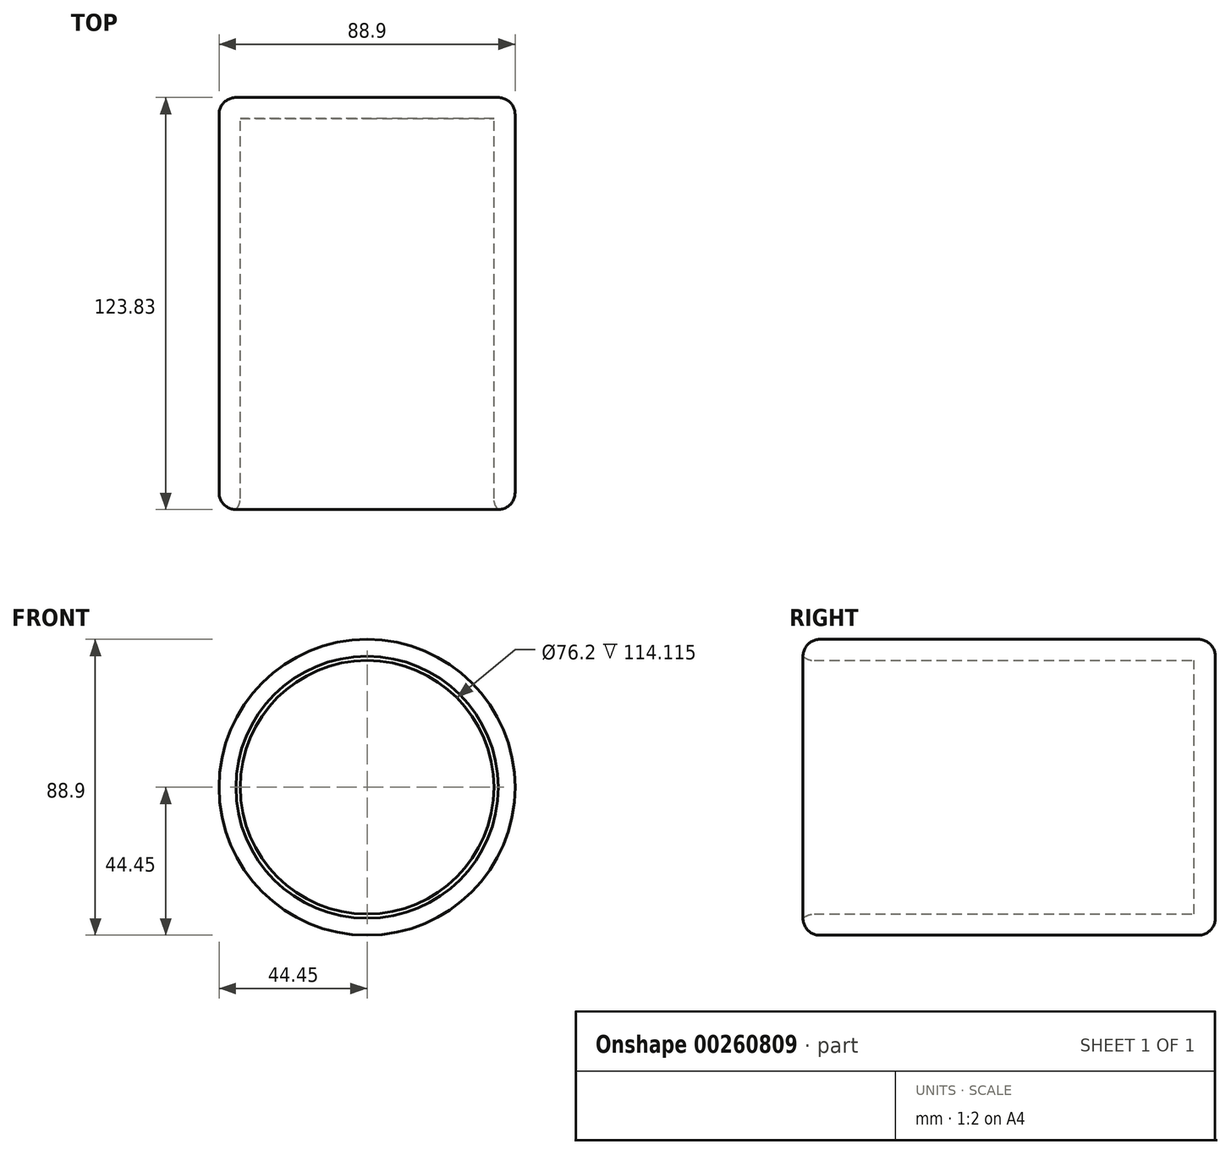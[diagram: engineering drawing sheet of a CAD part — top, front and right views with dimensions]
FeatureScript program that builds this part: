
annotation { "Feature Type Name" : "Feature", "Feature Type Description" : "" }
export const myFeature = defineFeature(function(context is Context, id is Id, definition is map)
    precondition{}
    {
        {
            var Q0;
            Q0=qCreatedBy(makeId("Front.planeOp"),FACE);
            var sketch = newSketch(context, id + "F0", { "sketchPlane" : qUnion([Q0])});
            skCircle(sketch, "E0", {"center": v(0, 0) * mm, "radius": 44.45 * mm});
            skCircle(sketch, "E1", {"center": v(0, 0) * mm, "radius": 38.1 * mm});
            skSolve(sketch);
        }
        {
            var Q0;
            Q0=makeQuery(id+"F0.imprint","IMPRINT",FACE,{"disambiguationData":[TD([[makeQuery(id+"F0.imprint","IMPRINT",EDGE,{"derivedFrom":sQuery(id+"F0.wireOp",EDGE,"E0")}),1.0]])]});
            extrude(context, id + "F1", {"entities" : qUnion([Q0]), "depth" : 123.82 * mm});
        }
        {
            var Q0;
            Q0=qCreatedBy(makeId("Front.planeOp"),FACE);
            var sketch = newSketch(context, id + "F2", { "sketchPlane" : qUnion([Q0])});
            skCircle(sketch, "E2", {"center": v(0, 0) * mm, "radius": 44.45 * mm});
            skSolve(sketch);
        }
        {
            var Q0;
            Q0=makeQuery(id+"F2.imprint","IMPRINT",FACE,{"disambiguationData":[TD([[makeQuery(id+"F2.imprint","IMPRINT",EDGE,{"derivedFrom":sQuery(id+"F2.wireOp",EDGE,"E2")}),1.0]])]});
            extrude(context, id + "F3", {"entities" : qUnion([Q0]), "operationType" : NewBodyOperationType.ADD, "depth" : 6.35 * mm});
        }
        {
            var Q0;
            Q0=makeQuery(id+"F1.opExtrude","SWEPT_FACE",FACE,{"disambiguationData":[OSD([sQuery(id+"F0.wireOp",EDGE,"E0")])]});
            var Q1;
            Q1=makeQuery(id+"F1.opExtrude","CAP_EDGE",EDGE,{"disambiguationData":[OSD([sQuery(id+"F0.wireOp",EDGE,"E0")])],"isStart":false});
            fillet(context, id + "F4", {"entities" : qUnion([Q0, Q1]), "radius" : 5.08 * mm, "tangentPropagation" : true, "allowEdgeOverflow" : false});
        }
        {
            var Q0;
            Q0=makeQuery(id+"F1.opExtrude","CAP_EDGE",EDGE,{"disambiguationData":[OSD([sQuery(id+"F0.wireOp",EDGE,"E1")])],"isStart":false});
            var Q1;
            {var subQ0=sQuery(id+"F0.wireOp",EDGE,"E0");Q1=makeQuery(id+"F4.opFillet","BLEND_EDGE",EDGE,{"blendedFrom":[makeQuery(id+"F1.opExtrude","CAP_EDGE",EDGE,{"disambiguationData":[OSD([subQ0])],"isStart":false}),makeQuery(id+"F1.opExtrude","CAP_FACE",FACE,{"disambiguationData":[OSD([subQ0,sQuery(id+"F0.wireOp",EDGE,"E1")])],"isStart":false})],"blendedInto":[makeQuery(id+"F1.opExtrude","CAP_FACE",FACE,{"disambiguationData":[OSD([subQ0,sQuery(id+"F0.wireOp",EDGE,"E1")])],"isStart":false})]});}
            fillet(context, id + "F5", {"entities" : qUnion([Q0, Q1]), "radius" : 5.08 * mm, "tangentPropagation" : true, "allowEdgeOverflow" : false});
        }
    });
